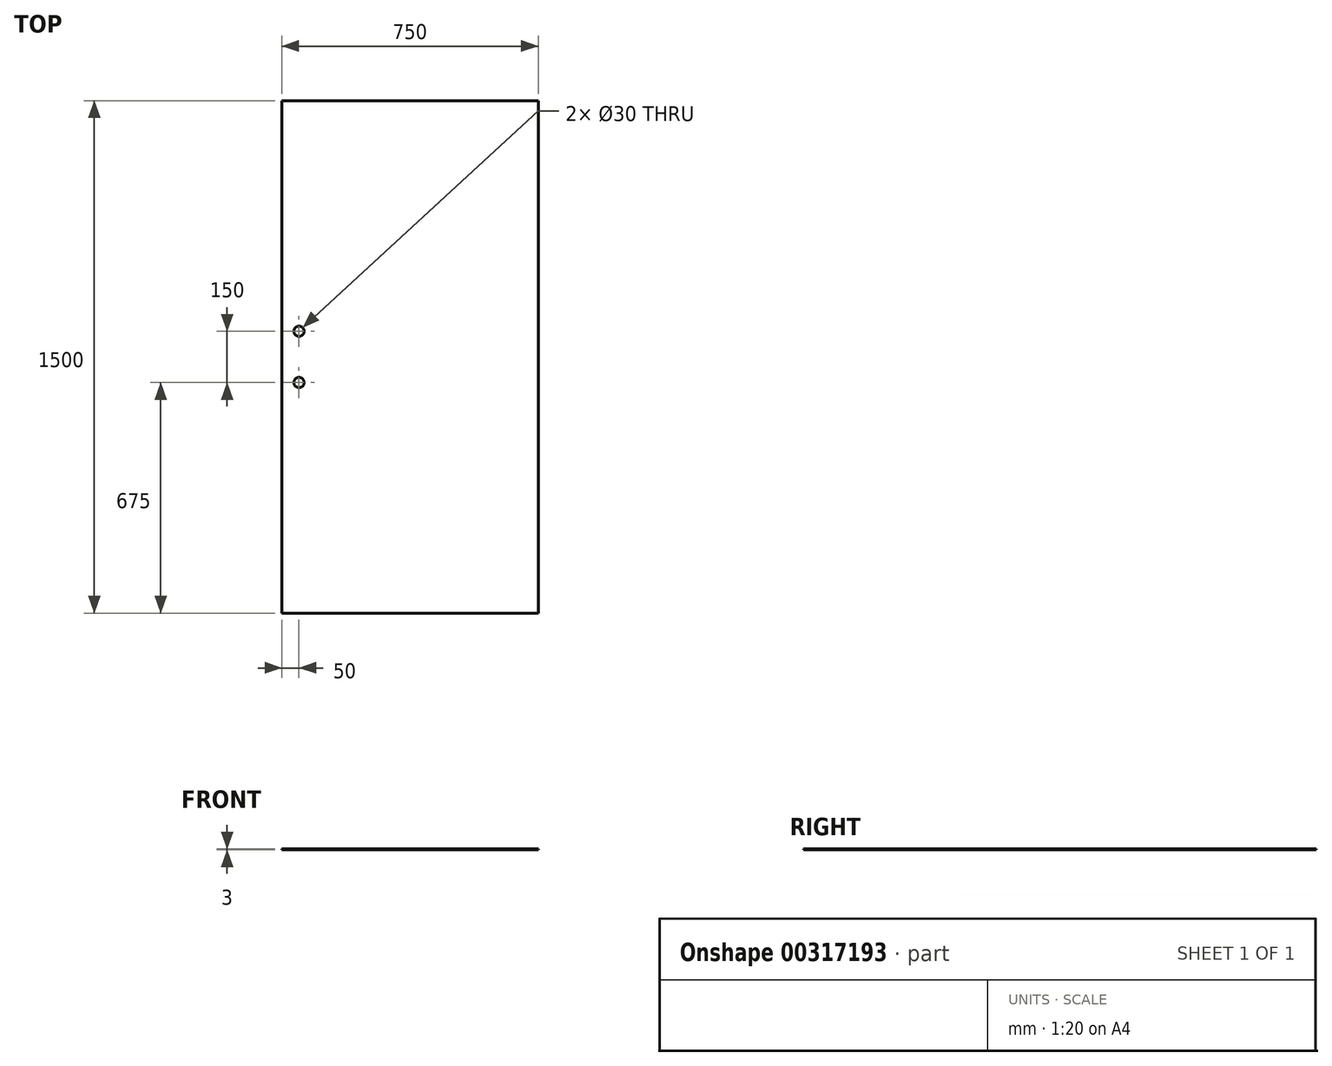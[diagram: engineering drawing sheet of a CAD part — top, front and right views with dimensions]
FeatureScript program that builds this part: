
annotation { "Feature Type Name" : "Feature", "Feature Type Description" : "" }
export const myFeature = defineFeature(function(context is Context, id is Id, definition is map)
    precondition{}
    {
        {
            var Q0;
            Q0=qCreatedBy(makeId("Top.planeOp"),FACE);
            var sketch = newSketch(context, id + "F0", { "sketchPlane" : qUnion([Q0])});
            skLineSegment(sketch, "E0.bottom", {"start": v(-375, 750) * mm, "end": v(375, 750) * mm});
            skLineSegment(sketch, "E0.top", {"start": v(-375, -750) * mm, "end": v(375, -750) * mm});
            skLineSegment(sketch, "E0.left", {"start": v(-375, 750) * mm, "end": v(-375, -750) * mm});
            skLineSegment(sketch, "E0.right", {"start": v(375, 750) * mm, "end": v(375, -750) * mm});
            skLineSegment(sketch, "E1", {"start": v(375, 750) * mm, "end": v(-375, -750) * mm, "construction": true});
            skSolve(sketch);
        }
        {
            var Q0;
            Q0 = qSketchRegion(id + "F0", true);
            extrude(context, id + "F1", {"entities" : qUnion([Q0]), "depth" : 3 * mm});
        }
        {
            var Q0;
            Q0=makeQuery(id+"F1.opExtrude","CAP_FACE",FACE,{"disambiguationData":[OSD([sQuery(id+"F0.wireOp",EDGE,"E0.bottom"),sQuery(id+"F0.wireOp",EDGE,"E0.top"),sQuery(id+"F0.wireOp",EDGE,"E0.left"),sQuery(id+"F0.wireOp",EDGE,"E0.right")])],"isStart":false});
            var sketch = newSketch(context, id + "F2", { "sketchPlane" : qUnion([Q0])});
            skCircle(sketch, "E2", {"center": v(-325, 75) * mm, "radius": 15 * mm});
            skCircle(sketch, "E3", {"center": v(-325, -75) * mm, "radius": 15 * mm});
            skLineSegment(sketch, "E4", {"start": v(-325, 75) * mm, "end": v(-325, -75) * mm, "construction": true});
            skLineSegment(sketch, "E5", {"start": v(-325, 0) * mm, "end": v(0, 0) * mm, "construction": true});
            skSolve(sketch);
        }
        {
            var Q0;
            Q0 = qSketchRegion(id + "F2", true);
            extrude(context, id + "F3", {"entities" : qUnion([Q0]), "operationType" : NewBodyOperationType.REMOVE, "oppositeDirection" : true, "depth" : 25 * mm});
        }
    });
